# Revit family: LAMP_OCULT SYSTEM SPOTLIGHT 1000 (DALI)
name_source: partatom
category: Luminarias
revit_build: Autodesk Revit 2015 (Build: 20140606_1530(x64)
units: mm (PartAtom-declared; Revit-internal decimal feet)

## types (16) — shared parameters
CRI = 80
Comentarios de tipo = Availability of tilting between 0º and 90º, rotation between 0º and 355º and change ring color when placed in a project.
Diameter = 40 mm  [stored 0.131234 ft]
Elevación por defecto = 1219 mm
Fabricante = LAMP
Gear = Adjustable DALI
Height = 78 mm  [stored 0.255906 ft]
Installation instructions = https://www.lamp.es
Insulation class = I
Last update = 31/07/2019
Luminaire type = Indoor - Spotlight
MacAdam = 3
Manufacturer URL = http://www.lamp.es
Manufacturer country = Spain
Manufacturer name = LAMP
Material suspension = Panel de metal
Model explanation = Availability of tilting between 0º and 90º, rotation between 0º and 355º and change ring color when placed in a project.
Power = 7 W
Power Supply = 100-240V 50/60Hz
Product URL = https://www.lamp.es
Product datasheet = http://www.lamp.es
Protection rating = IP20

## per-type parameters (varying)
| type | Descripción | Efficacy | Finish | IEE | Initial color | Initial intensity | LED Lifetime | Lamp | Material perfil | Modelo | Photometric web file | Plum | Product code | Type | Weight |
| 498LM 3000 SUPER SPOT BLACK | OCULT SYS. SPOT 1000 WW SSP DALI BK/BK. | 66 lm/W | Texturised black RAL 9011 | A+ | 3000 K | 498 lm | 50.000 L90 | HIGH POWER LED | LAMP_Aluminio Ocult Pendular NG | OS1SP10SS830DBB | Modelo spotlight 1000 : 498LM 3000 SUPER SPOT BLACK | 8 W | OS1SP10SS830DBB | HIGH POWER CREE | 0.85 kg |
| 498LM 3000 SUPER SPOT WHITE | OCULT SYS. SPOT 1000 WW SSP DALI BK/WH. | 66 lm/W | Texturised matt white | A+ | 3000 K | 498 lm | 50.000 L90 | HIGH POWER LED | LAMP_Aluminio Ocult Pendular BL | OS1SP10SS830DBW | Modelo spotlight 1000 : 498LM 3000 SUPER SPOT WHITE | 8 W | OS1SP10SS830DBW | HIGH POWER CREE | 0.85 kg |
| 537LM 4000 SUPER SPOT BLACK | OCULT SYS. SPOT 1000 NW SSP DALI BK/BK. | 71 lm/W | Texturised black RAL 9011 | A+ | 4000 K | 537 lm | 50.000 L90 | HIGH POWER LED | LAMP_Aluminio Ocult Pendular NG | OS1SP10SS840DBB | Modelo spotlight 1000 : 537LM 4000 SUPER SPOT BLACK | 8 W | OS1SP10SS840DBB | HIGH POWER CREE | 0.85 kg |
| 537LM 4000 SUPER SPOT WHITE | OCULT SYS. SPOT 1000 NW SSP DALI BK/WH. | 71 lm/W | Texturised matt white | A+ | 4000 K | 537 lm | 50.000 L90 | HIGH POWER LED | LAMP_Aluminio Ocult Pendular BL | OS1SP10SS840DBW | Modelo spotlight 1000 : 537LM 4000 SUPER SPOT WHITE | 8 W | OS1SP10SS840DBW | HIGH POWER CREE | 0.85 kg |
| 637LM 3000 FLOOD BLACK | OCULT SYS. SPOT 1000 WW FL DALI BK/BK. | 75 lm/W | Texturised black RAL 9011 | A+ | 3000 K | 637 lm | 50.000 L90 B10 | COB LED | LAMP_Aluminio Ocult Pendular NG | OS1SP10FL830DBB | Modelo spotlight 1000 : 637LM 3000 FLOOD BLACK | 9 W | OS1SP10FL830DBB | COB PHILIPS | 0.80 kg |
| 637LM 3000 FLOOD WHITE | OCULT SYS. SPOT 1000 WW FL DALI BK/WH. | 75 lm/W | Texturised matt white | A+ | 3000 K | 637 lm | 50.000 L90 B10 | COB LED | LAMP_Aluminio Ocult Pendular BL | OS1SP10FL830DBW | Modelo spotlight 1000 : 637LM 3000 FLOOD WHITE | 9 W | OS1SP10FL830DBW | COB PHILIPS | 0.80 kg |
| 670LM 3000 SPOT BLACK | OCULT SYS. SPOT 1000 WW SP DALI BK/BK. | 79 lm/W | Texturised black RAL 9011 | A+ | 3000 K | 670 lm | 50.000 L90 B10 | COB LED | LAMP_Aluminio Ocult Pendular NG | OS1SP10SP830DBB | Modelo spotlight 1000 : 670LM 3000 SPOT BLACK | 9 W | OS1SP10SP830DBB | COB PHILIPS | 0.80 kg |
| 670LM 3000 SPOT WHITE | OCULT SYS. SPOT 1000 WW SP DALI BK/WH. | 79 lm/W | Texturised matt white | A+ | 3000 K | 670 lm | 50.000 L90 B10 | COB LED | LAMP_Aluminio Ocult Pendular BL | OS1SP10SP830DBW | Modelo spotlight 1000 : 670LM 3000 SPOT WHITE | 9 W | OS1SP10SP830DBW | COB PHILIPS | 0.80 kg |
| 675LM 4000 FLOOD BLACK | OCULT SYS. SPOT 1000 NW FL DALI BK/BK. | 79 lm/W | Texturised black RAL 9011 | A+ | 4000 K | 675 lm | 50.000 L90 B10 | COB LED | LAMP_Aluminio Ocult Pendular NG | OS1SP10FL840DBB | Modelo spotlight 1000 : 675LM 4000 FLOOD BLACK | 9 W | OS1SP10FL840DBB | COB PHILIPS | 0.80 kg |
| 675LM 4000 FLOOD WHITE | OCULT SYS. SPOT 1000 NW FL DALI BK/WH. | 79 lm/W | Texturised matt white | A+ | 4000 K | 675 lm | 50.000 L90 B10 | COB LED | LAMP_Aluminio Ocult Pendular BL | OS1SP10FL840DBW | Modelo spotlight 1000 : 675LM 4000 FLOOD WHITE | 9 W | OS1SP10FL840DBW | COB PHILIPS | 0.80 kg |
| 699LM 3000 MEDIUM FLOOD BLACK | OCULT SYS. SPOT 1000 WW MFL DALI BK/BK. | 82 lm/W | Texturised black RAL 9011 | A++ | 3000 K | 699 lm | 50.000 L90 B10 | COB LED | LAMP_Aluminio Ocult Pendular NG | OS1SP10MF830DBB | Modelo spotlight 1000 : 699LM 3000 MEDIUM FLOOD BLACK | 9 W | OS1SP10MF830DBB | COB PHILIPS | 0.80 kg |
| 699LM 3000 MEDIUM FLOOD WHITE | OCULT SYS. SPOT 1000 WW MFL DALI BK/WH. | 82 lm/W | Texturised matt white | A++ | 3000 K | 699 lm | 50.000 L90 B10 | COB LED | LAMP_Aluminio Ocult Pendular BL | OS1SP10MF830DBW | Modelo spotlight 1000 : 699LM 3000 MEDIUM FLOOD WHITE | 9 W | OS1SP10MF830DBW | COB PHILIPS | 0.80 kg |
| 710LM 4000 SPOT BLACK | OCULT SYS. SPOT 1000 NW SP DALI BK/BK. | 84 lm/W | Texturised black RAL 9011 | A+ | 4000 K | 710 lm | 50.000 L90 B10 | COB LED | LAMP_Aluminio Ocult Pendular NG | OS1SP10SP840DBB | Modelo spotlight 1000 : 710LM 4000 SPOT BLACK | 9 W | OS1SP10SP840DBB | COB PHILIPS | 0.80 kg |
| 710LM 4000 SPOT WHITE | OCULT SYS. SPOT 1000 NW SP DALI BK/WH. | 84 lm/W | Texturised matt white | A+ | 4000 K | 710 lm | 50.000 L90 B10 | COB LED | LAMP_Aluminio Ocult Pendular BL | OS1SP10SP840DBW | Modelo spotlight 1000 : 710LM 4000 SPOT WHITE | 9 W | OS1SP10SP840DBW | COB PHILIPS | 0.80 kg |
| 740LM 4000 MEDIUM FLOOD BLACK | OCULT SYS. SPOT 1000 NW MFL DALI BK/BK. | 87 lm/W | Texturised black RAL 9011 | A++ | 4000 K | 740 lm | 50.000 L90 B10 | COB LED | LAMP_Aluminio Ocult Pendular NG | OS1SP10MF840DBB | Modelo spotlight 1000 : 740LM 4000 MEDIUM FLOOD BLACK | 9 W | OS1SP10MF840DBB | COB PHILIPS | 0.80 kg |
| 740LM 4000 MEDIUM FLOOD WHITE | OCULT SYS. SPOT 1000 NW MFL DALI BK/WH. | 87 lm/W | Texturised matt white | A++ | 4000 K | 740 lm | 50.000 L90 B10 | COB LED | LAMP_Aluminio Ocult Pendular BL | OS1SP10MF840DBW | Modelo spotlight 1000 : 740LM 4000 MEDIUM FLOOD WHITE | 9 W | OS1SP10MF840DBW | COB PHILIPS | 0.80 kg |

note: [stored X ft] marks values corroborated as IEEE doubles in the binary element streams (Revit-internal decimal feet)
